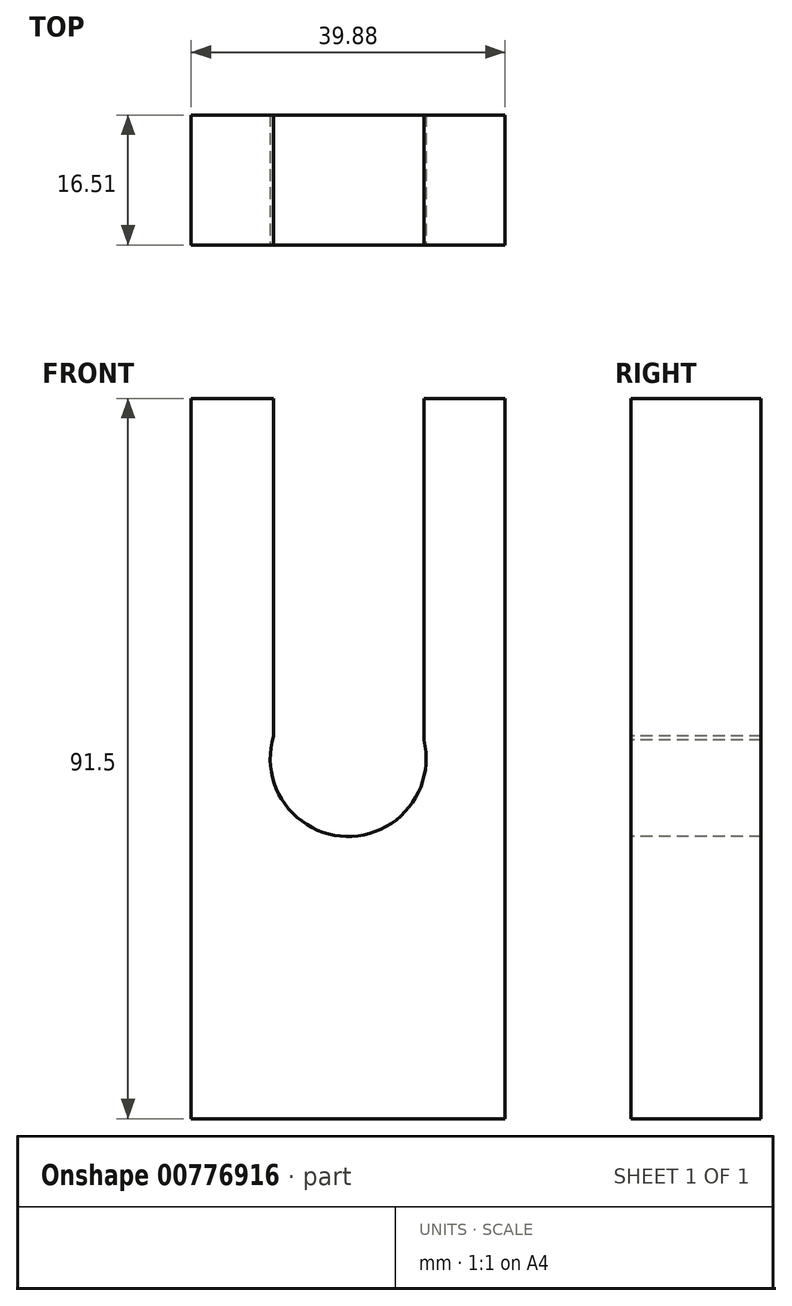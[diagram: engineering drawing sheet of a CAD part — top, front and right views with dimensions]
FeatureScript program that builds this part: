
annotation { "Feature Type Name" : "Feature", "Feature Type Description" : "" }
export const myFeature = defineFeature(function(context is Context, id is Id, definition is map)
    precondition{}
    {
        {
            var Q0;
            Q0=qCreatedBy(makeId("Front.planeOp"),FACE);
            var sketch = newSketch(context, id + "F0", { "sketchPlane" : qUnion([Q0])});
            skLineSegment(sketch, "E0.bottom", {"start": v(19.94, 45.75) * mm, "end": v(-19.94, 45.75) * mm});
            skLineSegment(sketch, "E0.top", {"start": v(19.94, -45.75) * mm, "end": v(-19.94, -45.75) * mm});
            skLineSegment(sketch, "E0.left", {"start": v(19.94, 45.75) * mm, "end": v(19.94, -45.75) * mm});
            skLineSegment(sketch, "E0.right", {"start": v(-19.94, 45.75) * mm, "end": v(-19.94, -45.75) * mm});
            skPoint(sketch, "E0.middle", {"position": v(0, 0) * mm});
            skSolve(sketch);
        }
        {
            var Q0;
            Q0 = qSketchRegion(id + "F0", true);
            extrude(context, id + "F1", {"entities" : qUnion([Q0]), "oppositeDirection" : true, "depth" : 16.5 * mm, "offsetDistance" : 25.4 * mm});
        }
        {
            var Q0;
            Q0=makeQuery(id+"F1.opExtrude","CAP_FACE",FACE,{"disambiguationData":[OSD([sQuery(id+"F0.wireOp",EDGE,"E0.bottom"),sQuery(id+"F0.wireOp",EDGE,"E0.top"),sQuery(id+"F0.wireOp",EDGE,"E0.left"),sQuery(id+"F0.wireOp",EDGE,"E0.right")])],"isStart":true});
            var sketch = newSketch(context, id + "F2", { "sketchPlane" : qUnion([Q0])});
            skCircle(sketch, "E1", {"center": v(0, 0) * mm, "radius": 9.9 * mm});
            skSolve(sketch);
        }
        {
            var Q0;
            Q0 = qSketchRegion(id + "F2", true);
            extrude(context, id + "F3", {"entities" : qUnion([Q0]), "operationType" : NewBodyOperationType.REMOVE, "oppositeDirection" : true, "depth" : 39.88 * mm, "offsetDistance" : 25.4 * mm});
        }
        {
            var Q0;
            Q0=qCreatedBy(makeId("Front.planeOp"),FACE);
            var sketch = newSketch(context, id + "F4", { "sketchPlane" : qUnion([Q0])});
            skLineSegment(sketch, "E2.bottom", {"start": v(-9.49, 0) * mm, "end": v(9.61, 0) * mm});
            skLineSegment(sketch, "E2.top", {"start": v(-9.49, 47.55) * mm, "end": v(9.61, 47.55) * mm});
            skLineSegment(sketch, "E2.left", {"start": v(-9.49, 0) * mm, "end": v(-9.49, 47.55) * mm});
            skLineSegment(sketch, "E2.right", {"start": v(9.61, 0) * mm, "end": v(9.61, 47.55) * mm});
            skSolve(sketch);
        }
        {
            var Q0;
            Q0 = qSketchRegion(id + "F4", true);
            extrude(context, id + "F5", {"entities" : qUnion([Q0]), "operationType" : NewBodyOperationType.REMOVE, "oppositeDirection" : true, "depth" : 25.4 * mm, "offsetDistance" : 25.4 * mm});
        }
    });
